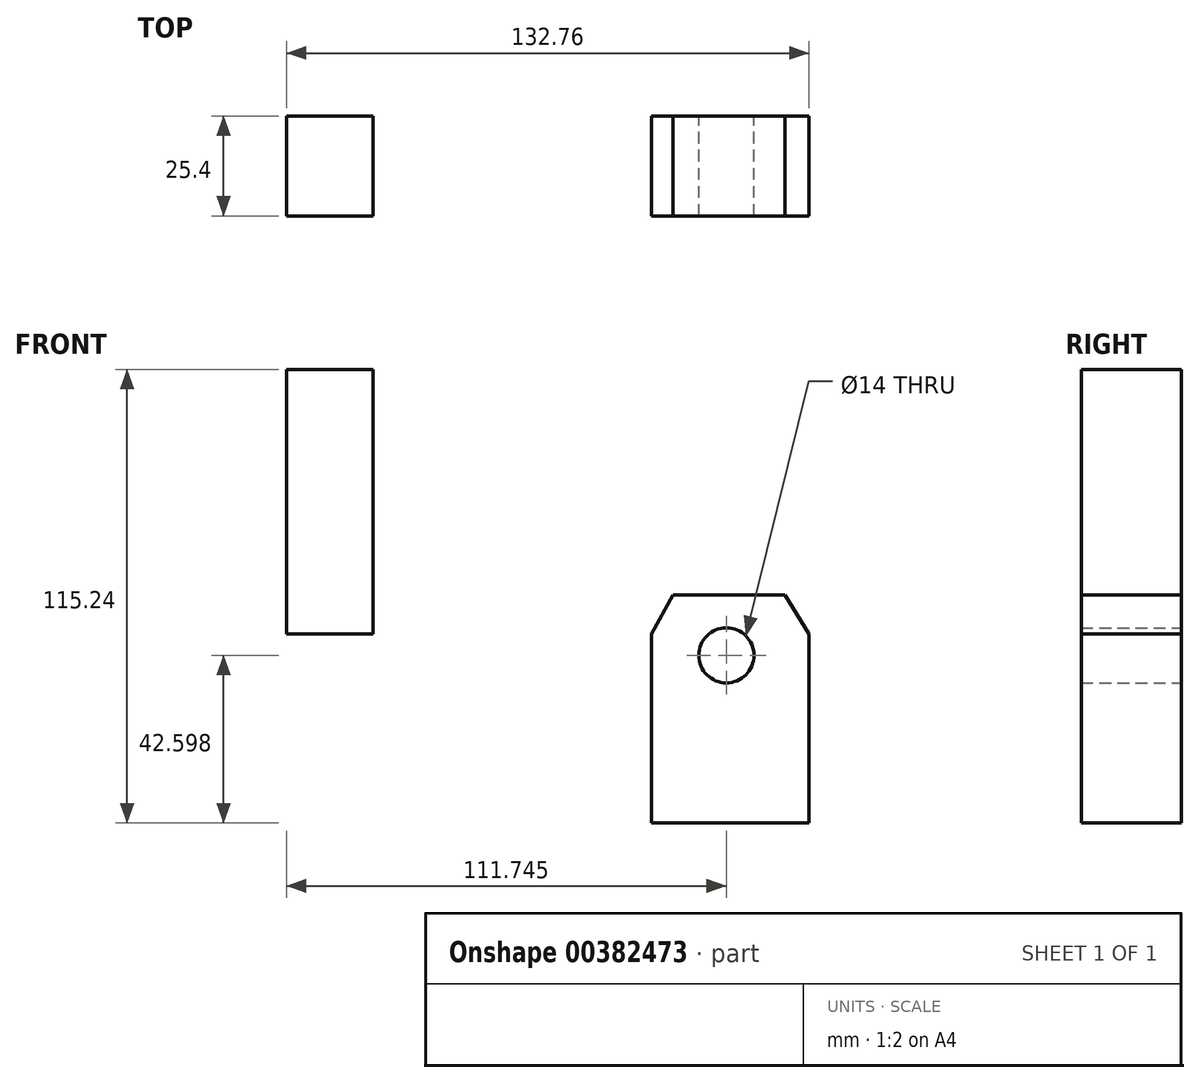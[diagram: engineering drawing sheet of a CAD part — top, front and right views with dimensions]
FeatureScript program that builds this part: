
annotation { "Feature Type Name" : "Feature", "Feature Type Description" : "" }
export const myFeature = defineFeature(function(context is Context, id is Id, definition is map)
    precondition{}
    {
        {
            var Q0;
            Q0=qCreatedBy(makeId("Front.planeOp"),FACE);
            var sketch = newSketch(context, id + "F0", { "sketchPlane" : qUnion([Q0])});
            skLineSegment(sketch, "E0", {"start": v(-68.53, 0) * mm, "end": v(-68.53, 56.26) * mm});
            skLineSegment(sketch, "E1", {"start": v(-68.53, 56.26) * mm, "end": v(-46.53, 56.26) * mm});
            skLineSegment(sketch, "E2", {"start": v(-46.53, 56.26) * mm, "end": v(-46.53, 0) * mm});
            skLineSegment(sketch, "E3", {"start": v(-46.53, 0) * mm, "end": v(-68.53, 0) * mm});
            skLineSegment(sketch, "E4", {"start": v(-68.53, 56.26) * mm, "end": v(-68.53, 67.26) * mm});
            skLineSegment(sketch, "E5", {"start": v(-68.53, 67.26) * mm, "end": v(-46.53, 67.26) * mm});
            skLineSegment(sketch, "E6", {"start": v(-46.53, 67.26) * mm, "end": v(-46.53, 56.26) * mm});
            skLineSegment(sketch, "E7", {"start": v(24.23, 0) * mm, "end": v(24.23, -47.98) * mm});
            skLineSegment(sketch, "E8", {"start": v(24.23, -47.98) * mm, "end": v(64.23, -47.98) * mm});
            skLineSegment(sketch, "E9", {"start": v(64.23, -47.98) * mm, "end": v(64.23, 0) * mm});
            skCircle(sketch, "E10", {"center": v(43.22, -5.38) * mm, "radius": 7 * mm});
            skLineSegment(sketch, "E11", {"start": v(58.14, 10) * mm, "end": v(64.23, 0) * mm});
            skLineSegment(sketch, "E12", {"start": v(24.23, 0) * mm, "end": v(29.63, 10) * mm});
            skLineSegment(sketch, "E13", {"start": v(29.63, 10) * mm, "end": v(58.14, 10) * mm});
            skSolve(sketch);
        }
        {
            var Q0;
            Q0=makeQuery(id+"F0.imprint","IMPRINT",FACE,{"disambiguationData":[TD([[makeQuery(id+"F0.imprint","IMPRINT",EDGE,{"derivedFrom":sQuery(id+"F0.wireOp",EDGE,"E0")}),-1.0]])]});
            var Q1;
            Q1=makeQuery(id+"F0.imprint","IMPRINT",FACE,{"disambiguationData":[TD([[makeQuery(id+"F0.imprint","IMPRINT",EDGE,{"derivedFrom":sQuery(id+"F0.wireOp",EDGE,"E1")}),1.0]])]});
            var Q2;
            Q2=makeQuery(id+"F0.imprint","IMPRINT",FACE,{"disambiguationData":[TD([[makeQuery(id+"F0.imprint","IMPRINT",EDGE,{"derivedFrom":sQuery(id+"F0.wireOp",EDGE,"E7")}),1.0]])]});
            extrude(context, id + "F1", {"entities" : qUnion([Q0, Q1, Q2]), "depth" : 25.4 * mm});
        }
    });
